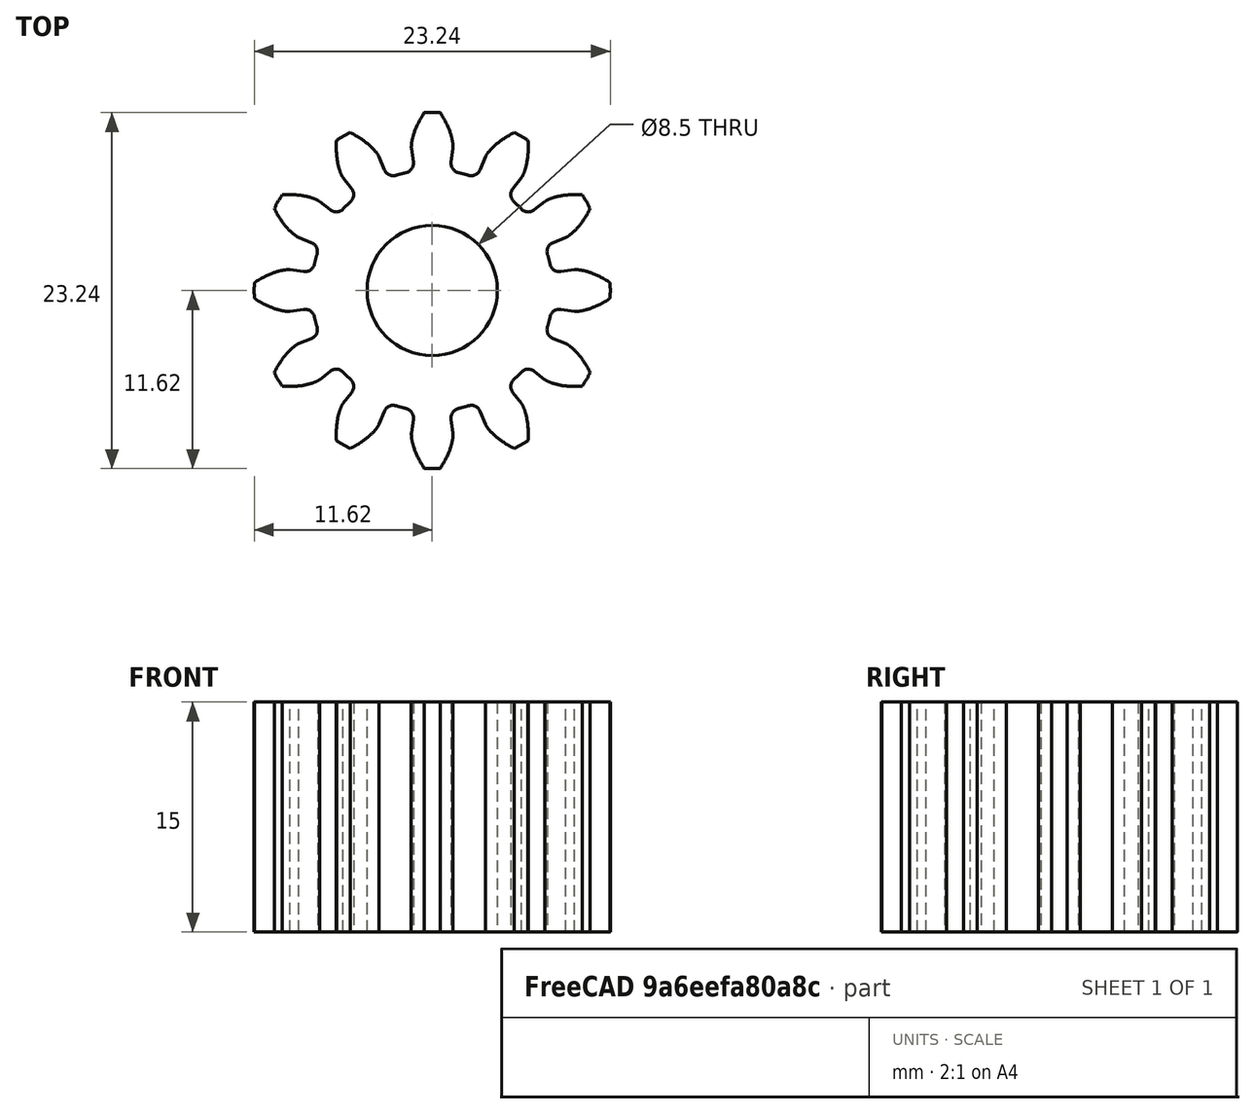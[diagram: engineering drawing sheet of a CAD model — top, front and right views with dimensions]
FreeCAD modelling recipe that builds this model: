
FCSTD DOCUMENT  (FreeCAD 0.18R4 (GitTag))
Label: Engranje 15mm 12 dientes 1.66
License: All rights reserved
LicenseURL: http://en.wikipedia.org/wiki/All_rights_reserved
objects: Part::Part2DObjectPython×1, PartDesign::Pad×1, Sketcher::SketchObject×1, PartDesign::Pocket×1, PartDesign::Body×1
note: 7 computed .brp shape members not serialized (recipe doc carries the construction recipe); baked Part::Feature solids carry a one-line shape summary decoded from their .brp

FEATURE [Part::Part2DObjectPython] InvoluteGear  # Draft 2D object (typed FeaturePython)
  ExternalGear = true
  HighPrecision = true
  Modules = 1.66
  NumberOfTeeth = 12
  PressureAngle = 20
FEATURE [PartDesign::Pad] Pad
  Length = 15
  Length2 = 100
  Profile = -> InvoluteGear
  Type = 0
FEATURE [Sketcher::SketchObject] Sketch
  MapMode = 5
  Placement = pos=(0,0,15) rot=(0,0,1;0rad)
  Support = -> [Pad]
  expr: Constraints[0] = 8.5 / 2
  sketch-geometry (1):
    g0: Circle CenterX=0 CenterY=0 CenterZ=0 NormalX=0 NormalY=0 NormalZ=1 AngleXU=0 Radius=4.25
  constraints (1):
    c: Radius(g0) = 4.25
FEATURE [PartDesign::Pocket] Pocket
  BaseFeature = -> Pad
  Length = 15
  Length2 = 100
  Profile = -> Sketch
  Type = 0
FEATURE [PartDesign::Body] Body
  Group = -> [InvoluteGear,Pad,Sketch,Pocket]
  Origin = -> Origin
  Tip = -> Pocket
